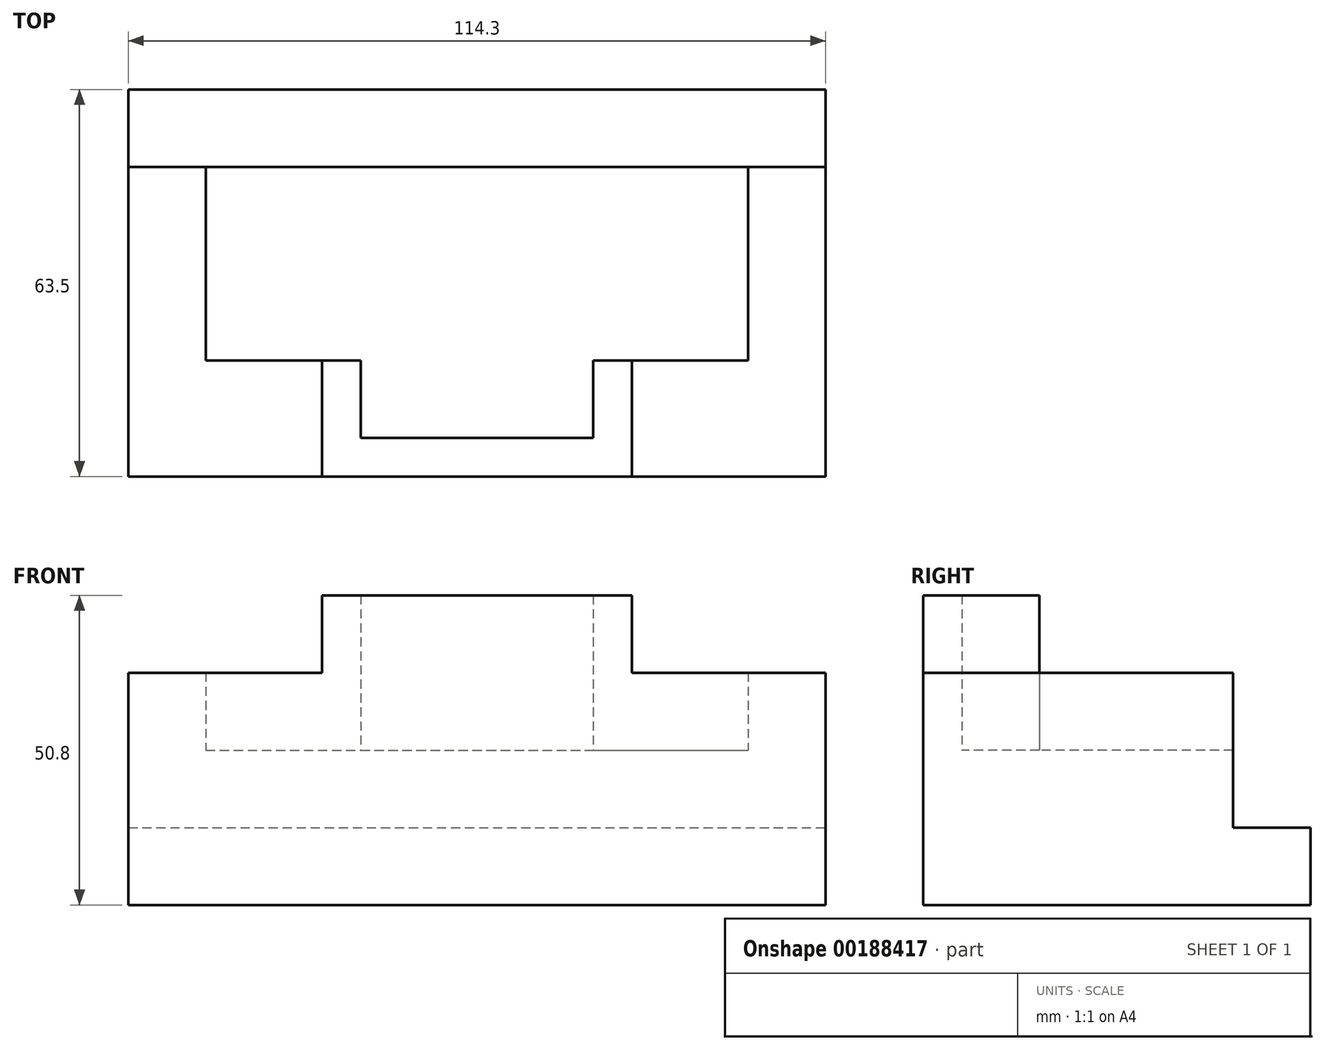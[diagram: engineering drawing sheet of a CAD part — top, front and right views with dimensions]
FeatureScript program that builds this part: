
annotation { "Feature Type Name" : "Feature", "Feature Type Description" : "" }
export const myFeature = defineFeature(function(context is Context, id is Id, definition is map)
    precondition{}
    {
        {
            var Q0;
            Q0=qCreatedBy(makeId("Top.planeOp"),FACE);
            var sketch = newSketch(context, id + "F0", { "sketchPlane" : qUnion([Q0])});
            skLineSegment(sketch, "E0.bottom", {"start": v(0, 0) * mm, "end": v(114.3, 0) * mm});
            skLineSegment(sketch, "E0.top", {"start": v(0, 63.5) * mm, "end": v(114.3, 63.5) * mm});
            skLineSegment(sketch, "E0.left", {"start": v(0, 0) * mm, "end": v(0, 63.5) * mm});
            skLineSegment(sketch, "E0.right", {"start": v(114.3, 0) * mm, "end": v(114.3, 63.5) * mm});
            skSolve(sketch);
        }
        {
            var Q0;
            Q0=makeQuery(id+"F0.imprint","IMPRINT",FACE,{"disambiguationData":[TD([[makeQuery(id+"F0.imprint","IMPRINT",EDGE,{"derivedFrom":sQuery(id+"F0.wireOp",EDGE,"E0.bottom")}),1.0]])]});
            extrude(context, id + "F1", {"entities" : qUnion([Q0]), "depth" : 12.7 * mm});
        }
        {
            var Q0;
            Q0=qCreatedBy(makeId("Top.planeOp"),FACE);
            cPlane(context, id + "F2", {"entities" : qUnion([Q0]), "cplaneType" : CPlaneType.OFFSET, "offset" : 12.7 * mm, "width" : 152.4 * mm, "height" : 152.4 * mm});
        }
        {
            var Q0;
            Q0=qCreatedBy(id+"F2.planeOp",FACE);
            var sketch = newSketch(context, id + "F3", { "sketchPlane" : qUnion([Q0])});
            skLineSegment(sketch, "E1.bottom", {"start": v(0, 0) * mm, "end": v(114.3, 0) * mm});
            skLineSegment(sketch, "E1.top", {"start": v(0, 50.8) * mm, "end": v(114.3, 50.8) * mm});
            skLineSegment(sketch, "E1.left", {"start": v(0, 0) * mm, "end": v(0, 50.8) * mm});
            skLineSegment(sketch, "E1.right", {"start": v(114.3, 0) * mm, "end": v(114.3, 50.8) * mm});
            skLineSegment(sketch, "E2", {"start": v(0, 50.8) * mm, "end": v(12.7, 50.8) * mm});
            skLineSegment(sketch, "E3", {"start": v(12.7, 50.8) * mm, "end": v(12.7, 19.05) * mm});
            skLineSegment(sketch, "E4", {"start": v(12.7, 19.05) * mm, "end": v(31.75, 19.05) * mm});
            skLineSegment(sketch, "E5", {"start": v(31.75, 19.05) * mm, "end": v(31.75, 0) * mm});
            skLineSegment(sketch, "E6", {"start": v(31.75, 0) * mm, "end": v(82.55, 0) * mm});
            skLineSegment(sketch, "E7", {"start": v(82.55, 0) * mm, "end": v(82.55, 19.05) * mm});
            skLineSegment(sketch, "E8", {"start": v(82.55, 19.05) * mm, "end": v(101.6, 19.05) * mm});
            skLineSegment(sketch, "E9", {"start": v(101.6, 19.05) * mm, "end": v(101.6, 50.8) * mm});
            skLineSegment(sketch, "E10", {"start": v(31.75, 19.05) * mm, "end": v(38.1, 19.05) * mm});
            skLineSegment(sketch, "E11", {"start": v(38.1, 19.05) * mm, "end": v(38.1, 6.35) * mm});
            skLineSegment(sketch, "E12", {"start": v(38.1, 6.35) * mm, "end": v(76.2, 6.35) * mm});
            skLineSegment(sketch, "E13", {"start": v(76.2, 6.35) * mm, "end": v(76.2, 19.05) * mm});
            skLineSegment(sketch, "E14", {"start": v(76.2, 19.05) * mm, "end": v(82.55, 19.05) * mm});
            skSolve(sketch);
        }
        {
            var Q0;
            {var subQ0=sQuery(id+"F3.wireOp",EDGE,"E3");Q0=makeQuery(id+"F3.imprint","IMPRINT",FACE,{"disambiguationData":[TD([[makeQuery(id+"F3.imprint","IMPRINT",EDGE,{"derivedFrom":subQ0}),1.0]])]});}
            extrude(context, id + "F4", {"entities" : qUnion([Q0]), "operationType" : NewBodyOperationType.ADD, "depth" : 12.7 * mm});
        }
        {
            var Q0;
            {var subQ1=sQuery(id+"F3.wireOp",EDGE,"E1.left");Q0=makeQuery(id+"F3.imprint","IMPRINT",FACE,{"disambiguationData":[TD([[makeQuery(id+"F3.imprint","IMPRINT",EDGE,{"derivedFrom":subQ1}),-1.0]])]});}
            var Q1;
            {var subQ0=sQuery(id+"F3.wireOp",EDGE,"E1.right");Q1=makeQuery(id+"F3.imprint","IMPRINT",FACE,{"disambiguationData":[TD([[makeQuery(id+"F3.imprint","IMPRINT",EDGE,{"derivedFrom":subQ0}),1.0]])]});}
            extrude(context, id + "F5", {"entities" : qUnion([Q0, Q1]), "operationType" : NewBodyOperationType.ADD, "depth" : 25.4 * mm});
        }
        {
            var Q0;
            Q0=makeQuery(id+"F3.imprint","IMPRINT",FACE,{"disambiguationData":[TD([[makeQuery(id+"F3.imprint","IMPRINT",EDGE,{"derivedFrom":sQuery(id+"F3.wireOp",EDGE,"E5")}),1.0]])]});
            extrude(context, id + "F6", {"entities" : qUnion([Q0]), "operationType" : NewBodyOperationType.ADD, "depth" : 38.1 * mm});
        }
    });
